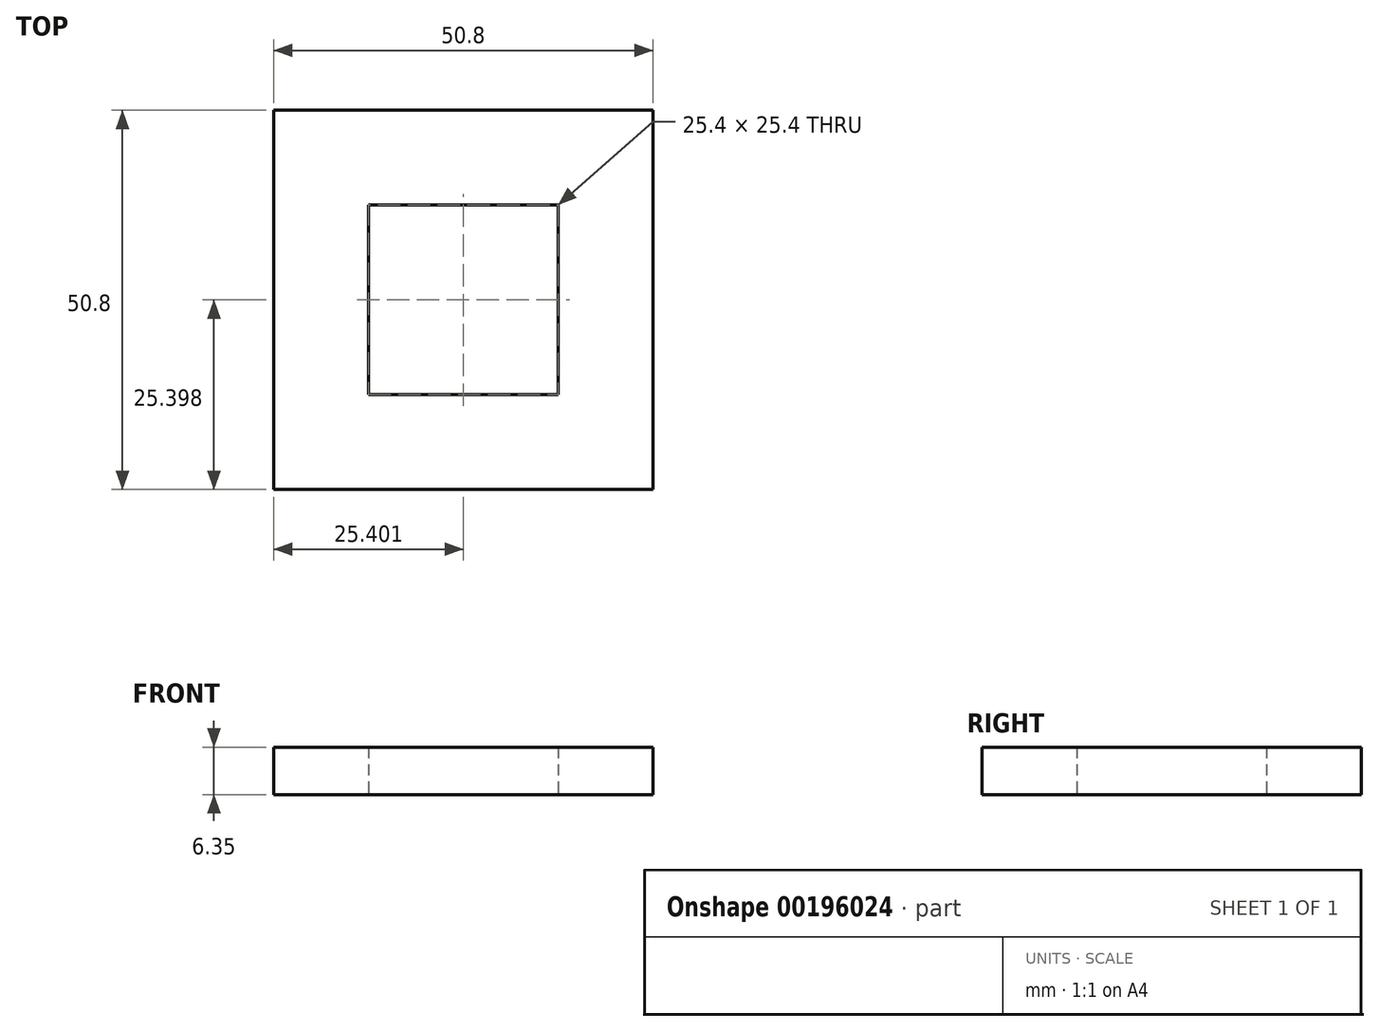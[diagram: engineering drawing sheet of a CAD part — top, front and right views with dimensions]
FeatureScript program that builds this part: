
annotation { "Feature Type Name" : "Feature", "Feature Type Description" : "" }
export const myFeature = defineFeature(function(context is Context, id is Id, definition is map)
    precondition{}
    {
        {
            var Q0;
            Q0=qCreatedBy(makeId("Top.planeOp"),FACE);
            var sketch = newSketch(context, id + "F0", { "sketchPlane" : qUnion([Q0])});
            skLineSegment(sketch, "E0.bottom", {"start": v(-20.9, 21.8) * mm, "end": v(29.9, 21.8) * mm});
            skLineSegment(sketch, "E0.top", {"start": v(-20.9, -29) * mm, "end": v(29.9, -29) * mm});
            skLineSegment(sketch, "E0.left", {"start": v(-20.9, 21.8) * mm, "end": v(-20.9, -29) * mm});
            skLineSegment(sketch, "E0.right", {"start": v(29.9, 21.8) * mm, "end": v(29.9, -29) * mm});
            skLineSegment(sketch, "E1.0", {"start": v(-8.2, 9.1) * mm, "end": v(17.2, 9.1) * mm});
            skLineSegment(sketch, "E1.1", {"start": v(-8.2, 9.1) * mm, "end": v(-8.2, -16.3) * mm});
            skLineSegment(sketch, "E1.2", {"start": v(-8.2, -16.3) * mm, "end": v(17.2, -16.3) * mm});
            skLineSegment(sketch, "E1.3", {"start": v(17.2, 9.1) * mm, "end": v(17.2, -16.3) * mm});
            skSolve(sketch);
        }
        {
            var Q0;
            Q0=makeQuery(id+"F0.imprint","IMPRINT",FACE,{"disambiguationData":[TD([[makeQuery(id+"F0.imprint","IMPRINT",EDGE,{"derivedFrom":sQuery(id+"F0.wireOp",EDGE,"E0.bottom")}),-1.0]])]});
            extrude(context, id + "F1", {"entities" : qUnion([Q0]), "depth" : 6.35 * mm});
        }
    });
